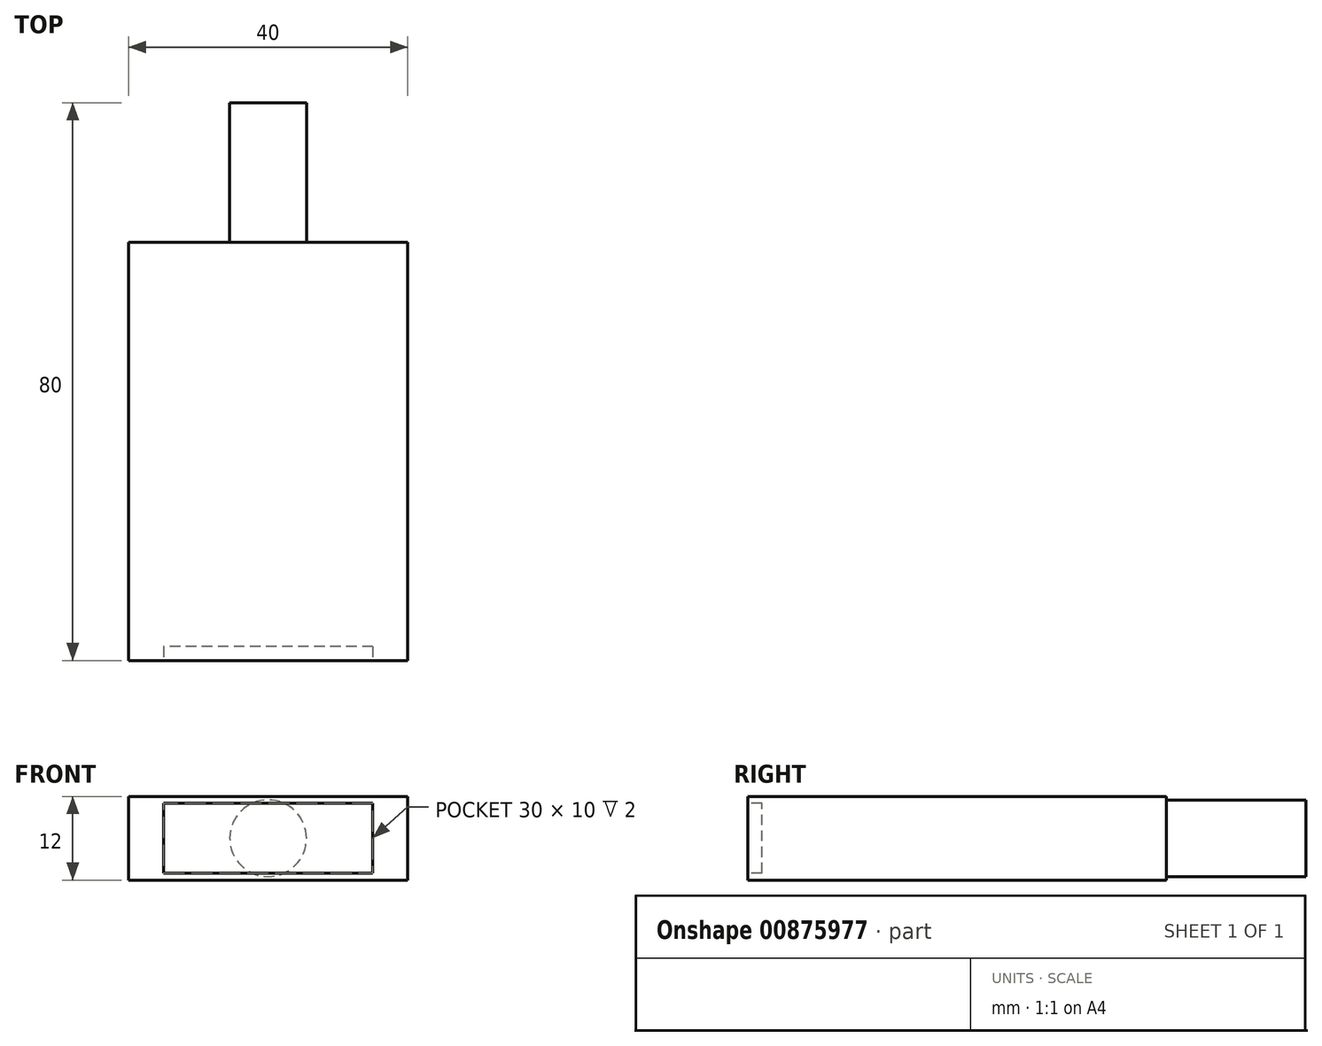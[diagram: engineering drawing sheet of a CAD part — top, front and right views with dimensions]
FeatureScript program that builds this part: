
annotation { "Feature Type Name" : "Feature", "Feature Type Description" : "" }
export const myFeature = defineFeature(function(context is Context, id is Id, definition is map)
    precondition{}
    {
        {
            var Q0;
            Q0=qCreatedBy(makeId("Top.planeOp"),FACE);
            var sketch = newSketch(context, id + "F0", { "sketchPlane" : qUnion([Q0])});
            skLineSegment(sketch, "E0.bottom", {"start": v(20, -30) * mm, "end": v(-20, -30) * mm});
            skLineSegment(sketch, "E0.top", {"start": v(20, 30) * mm, "end": v(-20, 30) * mm});
            skLineSegment(sketch, "E0.left", {"start": v(20, -30) * mm, "end": v(20, 30) * mm});
            skLineSegment(sketch, "E0.right", {"start": v(-20, -30) * mm, "end": v(-20, 30) * mm});
            skPoint(sketch, "E0.middle", {"position": v(0, 0) * mm});
            skSolve(sketch);
        }
        {
            var Q0;
            Q0 = qSketchRegion(id + "F0", true);
            extrude(context, id + "F1", {"entities" : qUnion([Q0]), "depth" : 12 * mm, "offsetDistance" : 25 * mm});
        }
        {
            var Q0;
            Q0=makeQuery(id+"F1.opExtrude","SWEPT_FACE",FACE,{"disambiguationData":[OSD([sQuery(id+"F0.wireOp",EDGE,"E0.bottom")])]});
            var sketch = newSketch(context, id + "F2", { "sketchPlane" : qUnion([Q0])});
            skLineSegment(sketch, "E1.bottom", {"start": v(15, 1) * mm, "end": v(-15, 1) * mm});
            skLineSegment(sketch, "E1.top", {"start": v(15, 11) * mm, "end": v(-15, 11) * mm});
            skLineSegment(sketch, "E1.left", {"start": v(15, 1) * mm, "end": v(15, 11) * mm});
            skLineSegment(sketch, "E1.right", {"start": v(-15, 1) * mm, "end": v(-15, 11) * mm});
            skPoint(sketch, "E1.middle", {"position": v(0, 6) * mm});
            skPoint(sketch, "E1.middle.positionSnap0", {"position": v(-20, 6) * mm});
            skPoint(sketch, "E1.centerSnap0", {"position": v(-20, 6) * mm});
            skSolve(sketch);
        }
        {
            var Q0;
            Q0=makeQuery(id+"F2.imprint","IMPRINT",FACE,{"disambiguationData":[TD([[makeQuery(id+"F2.imprint","IMPRINT",EDGE,{"derivedFrom":sQuery(id+"F2.wireOp",EDGE,"E1.bottom")}),-1.0]])]});
            extrude(context, id + "F3", {"entities" : qUnion([Q0]), "operationType" : NewBodyOperationType.REMOVE, "oppositeDirection" : true, "depth" : 2 * mm, "offsetDistance" : 25 * mm});
        }
        {
            var Q0;
            Q0=makeQuery(id+"F1.opExtrude","SWEPT_FACE",FACE,{"disambiguationData":[OSD([sQuery(id+"F0.wireOp",EDGE,"E0.top")])]});
            var sketch = newSketch(context, id + "F4", { "sketchPlane" : qUnion([Q0])});
            skCircle(sketch, "E2", {"center": v(0, 6) * mm, "radius": 5.5 * mm});
            skPoint(sketch, "E2.centerSnap0", {"position": v(-20, 6) * mm});
            skSolve(sketch);
        }
        {
            var Q0;
            Q0=makeQuery(id+"F4.imprint","IMPRINT",FACE,{"disambiguationData":[TD([[makeQuery(id+"F4.imprint","IMPRINT",EDGE,{"derivedFrom":sQuery(id+"F4.wireOp",EDGE,"E2")}),1.0]])]});
            extrude(context, id + "F5", {"entities" : qUnion([Q0]), "operationType" : NewBodyOperationType.ADD, "depth" : 20 * mm, "offsetDistance" : 25 * mm});
        }
    });
